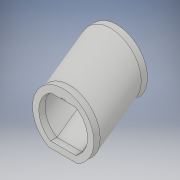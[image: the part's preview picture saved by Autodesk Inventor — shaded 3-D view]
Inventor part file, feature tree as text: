
AUTODESK INVENTOR PART (.ipt)
format: ipt  version: 2017 (Build 210142000, 142)  size: 224,256 bytes
history: native  units: in
note: dims shown in document units (in); Inventor stores cm internally (conversion verified against a paired STEP export)
features: sketch x4, extrude x4, sweep x2, plane x1
ambient origin geometry x8: Origin, YZ Plane, XZ Plane, XY Plane, X Axis, Y Axis, Z Axis, Center Point
bodies: Solid1 (feature_tree), Solid2 (feature_tree), Solid3 (feature_tree), Solid4 (feature_tree)
feature tree (11):
  sketch  "Sketch1"  dims[d0=6.6667in d1=4.0in d2=1.0in d3=1.0in d4=0.0in d12=8.0in]
  extrude  "connection top"  Depth=8.0in
  extrude  "light flat top"  Depth=8.0in
  plane  "Work Plane2"
  sketch  "Sketch6"  dims[d28=8.0in d29=0.3779in]
  sweep  "ramp"
  sweep  "light angle"
  extrude  "connection bottom"  TaperAngle=0.0deg  [1 undecoded]
  extrude  "light flat bottom"  Depth=1.0in TaperAngle=0.0deg
  sketch  "Sketch8"  dims[d34=0.5833in d35=0.0625in d36=0.0625in d37=0.125in]
  sketch  "Sketch9"  dims[d38=0.25in d39=0.125in d40=45.0deg d41=0.0892in d42=0.0884in d43=1.0in d44=0.0in d45=0.0in d46=0.0in d47=0.0in d48=0.0in d49=1.0in d50=0.0in d52=1.0in d53=0.0in]
note: 1 required parameter value undecoded (feature->parameter linkage not recoverable at this tier; creation-order binding heuristic only, values carry confidence <= 0.55)
